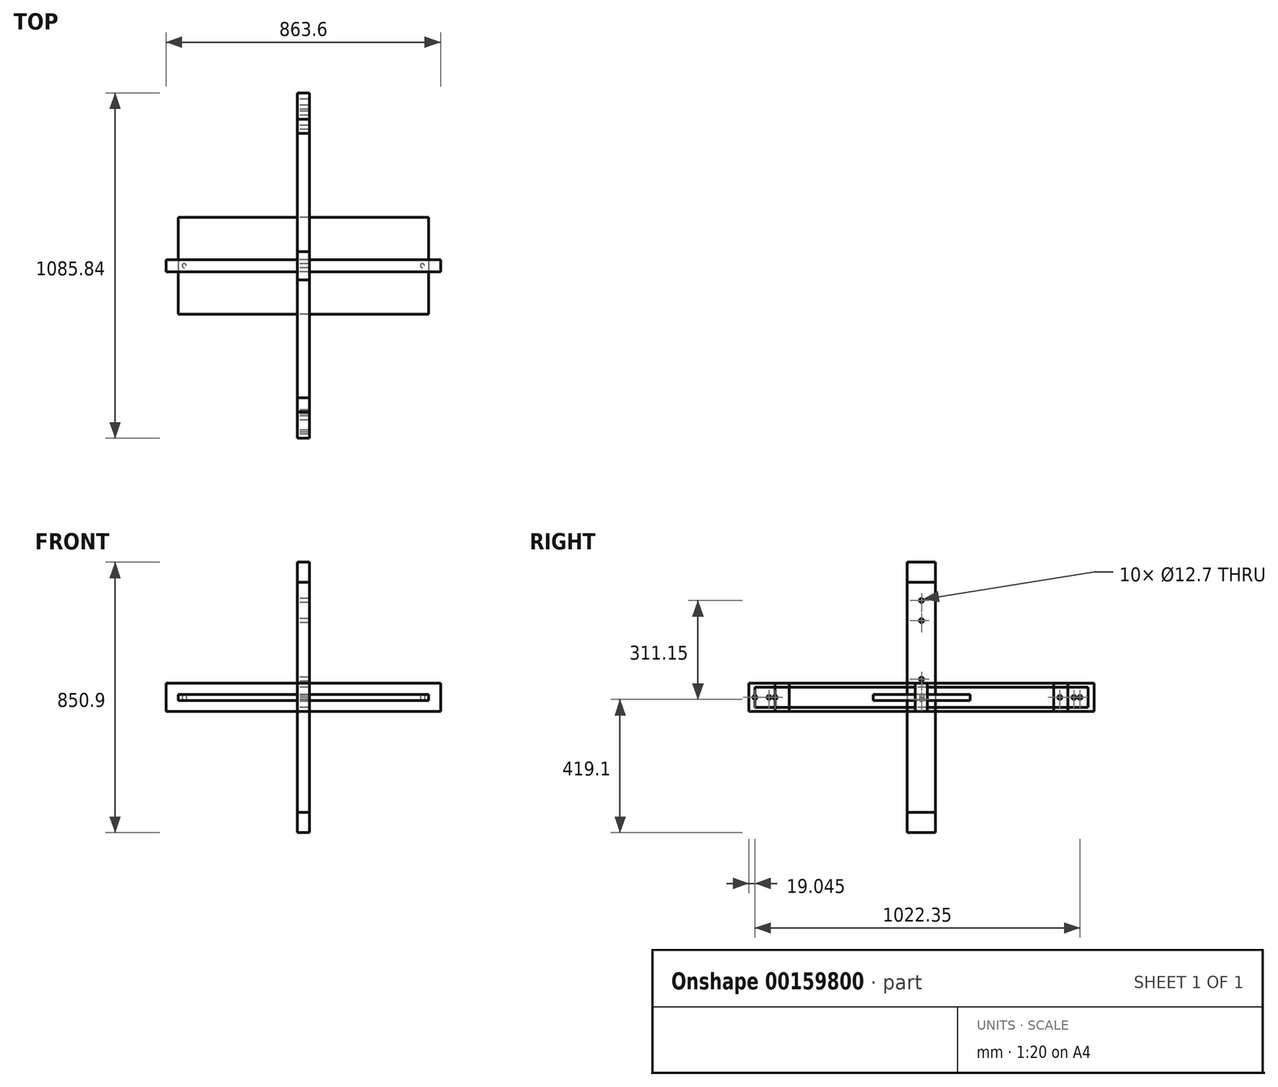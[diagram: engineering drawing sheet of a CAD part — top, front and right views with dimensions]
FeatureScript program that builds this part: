
annotation { "Feature Type Name" : "Feature", "Feature Type Description" : "" }
export const myFeature = defineFeature(function(context is Context, id is Id, definition is map)
    precondition{}
    {
        {
            var Q0;
            Q0=qCreatedBy(makeId("Front.planeOp"),FACE);
            var sketch = newSketch(context, id + "F0", { "sketchPlane" : qUnion([Q0])});
            skLineSegment(sketch, "E0.bottom", {"start": v(431.8, -44.45) * mm, "end": v(-431.8, -44.45) * mm});
            skLineSegment(sketch, "E0.top", {"start": v(431.8, 44.45) * mm, "end": v(-431.8, 44.45) * mm});
            skLineSegment(sketch, "E0.left", {"start": v(431.8, -44.45) * mm, "end": v(431.8, 44.45) * mm});
            skLineSegment(sketch, "E0.right", {"start": v(-431.8, -44.45) * mm, "end": v(-431.8, 44.45) * mm});
            skPoint(sketch, "E0.middle", {"position": v(0, 0) * mm});
            skSolve(sketch);
        }
        {
            var Q0;
            Q0 = qSketchRegion(id + "F0", true);
            extrude(context, id + "F1", {"entities" : qUnion([Q0]), "depth" : 38.1 * mm, "symmetric" : true});
        }
        {
            var Q0;
            Q0=qCreatedBy(makeId("Right.planeOp"),FACE);
            var sketch = newSketch(context, id + "F2", { "sketchPlane" : qUnion([Q0])});
            skLineSegment(sketch, "E1.bottom", {"start": v(542.93, -44.45) * mm, "end": v(-542.93, -44.45) * mm});
            skLineSegment(sketch, "E1.top", {"start": v(542.93, 44.45) * mm, "end": v(-542.93, 44.45) * mm});
            skLineSegment(sketch, "E1.left", {"start": v(542.93, -44.45) * mm, "end": v(542.93, 44.45) * mm});
            skLineSegment(sketch, "E1.right", {"start": v(-542.93, -44.45) * mm, "end": v(-542.93, 44.45) * mm});
            skPoint(sketch, "E1.middle", {"position": v(0, 0) * mm});
            skCircle(sketch, "E2", {"center": v(-523.88, 0) * mm, "radius": 6.35 * mm});
            skCircle(sketch, "E3", {"center": v(-460.38, 0) * mm, "radius": 6.35 * mm});
            skCircle(sketch, "E4", {"center": v(498.48, 0) * mm, "radius": 6.35 * mm});
            skPoint(sketch, "E4.centerSnap0", {"position": v(542.93, 0) * mm});
            skCircle(sketch, "E5", {"center": v(434.98, 0) * mm, "radius": 6.35 * mm});
            skSolve(sketch);
        }
        {
            var Q0;
            Q0 = qSketchRegion(id + "F2", true);
            extrude(context, id + "F3", {"entities" : qUnion([Q0]), "depth" : 38.1 * mm, "symmetric" : true});
        }
        {
            var Q0;
            Q0=qCreatedBy(makeId("Right.planeOp"),FACE);
            var sketch = newSketch(context, id + "F4", { "sketchPlane" : qUnion([Q0])});
            skLineSegment(sketch, "E6.bottom", {"start": v(-44.45, 361.95) * mm, "end": v(44.45, 361.95) * mm});
            skLineSegment(sketch, "E6.top", {"start": v(-44.45, -361.95) * mm, "end": v(44.45, -361.95) * mm});
            skLineSegment(sketch, "E6.left", {"start": v(-44.45, 361.95) * mm, "end": v(-44.45, -361.95) * mm});
            skLineSegment(sketch, "E6.right", {"start": v(44.45, 361.95) * mm, "end": v(44.45, -361.95) * mm});
            skPoint(sketch, "E6.middle", {"position": v(0, 0) * mm});
            skCircle(sketch, "E7", {"center": v(0, 304.8) * mm, "radius": 6.35 * mm});
            skCircle(sketch, "E8", {"center": v(0, 57.15) * mm, "radius": 6.35 * mm});
            skSolve(sketch);
        }
        {
            var Q0;
            Q0 = qSketchRegion(id + "F4", true);
            extrude(context, id + "F5", {"entities" : qUnion([Q0]), "depth" : 38.1 * mm, "symmetric" : true});
        }
        {
            var Q0;
            Q0=qCreatedBy(makeId("Right.planeOp"),FACE);
            var sketch = newSketch(context, id + "F6", { "sketchPlane" : qUnion([Q0])});
            skLineSegment(sketch, "E9.bottom", {"start": v(44.45, 425.45) * mm, "end": v(-44.45, 425.45) * mm});
            skLineSegment(sketch, "E9.top", {"start": v(44.45, -425.45) * mm, "end": v(-44.45, -425.45) * mm});
            skLineSegment(sketch, "E9.left", {"start": v(44.45, 425.45) * mm, "end": v(44.45, -425.45) * mm});
            skLineSegment(sketch, "E9.right", {"start": v(-44.45, 425.45) * mm, "end": v(-44.45, -425.45) * mm});
            skPoint(sketch, "E9.middle", {"position": v(0, 0) * mm});
            skCircle(sketch, "E10", {"center": v(0, 241.3) * mm, "radius": 6.35 * mm});
            skCircle(sketch, "E11", {"center": v(0, -6.35) * mm, "radius": 6.35 * mm});
            skSolve(sketch);
        }
        {
            var Q0;
            Q0 = qSketchRegion(id + "F6", true);
            extrude(context, id + "F7", {"entities" : qUnion([Q0]), "depth" : 38.1 * mm, "symmetric" : true});
        }
        {
            var Q0;
            Q0=qCreatedBy(makeId("Top.planeOp"),FACE);
            var sketch = newSketch(context, id + "F8", { "sketchPlane" : qUnion([Q0])});
            skLineSegment(sketch, "E12.bottom", {"start": v(393.7, 152.4) * mm, "end": v(-393.7, 152.4) * mm});
            skLineSegment(sketch, "E12.top", {"start": v(393.7, -152.4) * mm, "end": v(-393.7, -152.4) * mm});
            skLineSegment(sketch, "E12.left", {"start": v(393.7, 152.4) * mm, "end": v(393.7, -152.4) * mm});
            skLineSegment(sketch, "E12.right", {"start": v(-393.7, 152.4) * mm, "end": v(-393.7, -152.4) * mm});
            skPoint(sketch, "E12.middle", {"position": v(0, 0) * mm});
            skCircle(sketch, "E13", {"center": v(-374.65, 0) * mm, "radius": 6.35 * mm});
            skCircle(sketch, "E14", {"center": v(374.65, 0) * mm, "radius": 6.35 * mm});
            skPoint(sketch, "E14.centerSnap0", {"position": v(-393.7, 0) * mm});
            skSolve(sketch);
        }
        {
            var Q0;
            Q0 = qSketchRegion(id + "F8", true);
            extrude(context, id + "F9", {"entities" : qUnion([Q0]), "depth" : 19.05 * mm, "symmetric" : true});
        }
        {
            var Q0;
            Q0=qCreatedBy(makeId("Right.planeOp"),FACE);
            var sketch = newSketch(context, id + "F10", { "sketchPlane" : qUnion([Q0])});
            skLineSegment(sketch, "E15.bottom", {"start": v(523.88, -31.75) * mm, "end": v(-523.88, -31.75) * mm});
            skLineSegment(sketch, "E15.top", {"start": v(523.88, 31.75) * mm, "end": v(-523.88, 31.75) * mm});
            skLineSegment(sketch, "E15.left", {"start": v(523.88, -31.75) * mm, "end": v(523.88, 31.75) * mm});
            skLineSegment(sketch, "E15.right", {"start": v(-523.88, -31.75) * mm, "end": v(-523.88, 31.75) * mm});
            skPoint(sketch, "E15.middle", {"position": v(0, 0) * mm});
            skCircle(sketch, "E16", {"center": v(-479.43, 0) * mm, "radius": 6.35 * mm});
            skCircle(sketch, "E17", {"center": v(479.43, 0) * mm, "radius": 6.35 * mm});
            skPoint(sketch, "E17.centerSnap0", {"position": v(523.88, 0) * mm});
            skSolve(sketch);
        }
        {
            var Q0;
            Q0=makeQuery(id+"F10.imprint","IMPRINT",FACE,{"disambiguationData":[TD([[makeQuery(id+"F10.imprint","IMPRINT",EDGE,{"derivedFrom":sQuery(id+"F10.wireOp",EDGE,"E15.bottom")}),-1.0]])]});
            extrude(context, id + "F11", {"entities" : qUnion([Q0]), "depth" : 38.1 * mm, "symmetric" : true});
        }
        {
            var Q0;
            Q0=qCreatedBy(makeId("Right.planeOp"),FACE);
            var sketch = newSketch(context, id + "F12", { "sketchPlane" : qUnion([Q0])});
            skLineSegment(sketch, "E18.bottom", {"start": v(460.38, 44.45) * mm, "end": v(-460.38, 44.45) * mm});
            skLineSegment(sketch, "E18.top", {"start": v(460.38, -44.45) * mm, "end": v(-460.38, -44.45) * mm});
            skLineSegment(sketch, "E18.left", {"start": v(460.38, 44.45) * mm, "end": v(460.38, -44.45) * mm});
            skLineSegment(sketch, "E18.right", {"start": v(-460.38, 44.45) * mm, "end": v(-460.38, -44.45) * mm});
            skPoint(sketch, "E18.middle", {"position": v(0, 0) * mm});
            skSolve(sketch);
        }
        {
            var Q0;
            Q0=makeQuery(id+"F12.imprint","IMPRINT",FACE,{"disambiguationData":[TD([[makeQuery(id+"F12.imprint","IMPRINT",EDGE,{"derivedFrom":sQuery(id+"F12.wireOp",EDGE,"E18.bottom")}),1.0]])]});
            extrude(context, id + "F13", {"entities" : qUnion([Q0]), "depth" : 38.1 * mm, "symmetric" : true});
        }
        {
            var Q0;
            Q0=qCreatedBy(makeId("Right.planeOp"),FACE);
            var sketch = newSketch(context, id + "F14", { "sketchPlane" : qUnion([Q0])});
            skLineSegment(sketch, "E19.bottom", {"start": v(415.93, 44.45) * mm, "end": v(-415.93, 44.45) * mm});
            skLineSegment(sketch, "E19.top", {"start": v(415.93, -44.45) * mm, "end": v(-415.93, -44.45) * mm});
            skLineSegment(sketch, "E19.left", {"start": v(415.93, 44.45) * mm, "end": v(415.93, -44.45) * mm});
            skLineSegment(sketch, "E19.right", {"start": v(-415.93, 44.45) * mm, "end": v(-415.93, -44.45) * mm});
            skPoint(sketch, "E19.middle", {"position": v(0, 0) * mm});
            skSolve(sketch);
        }
        {
            var Q0;
            Q0 = qSketchRegion(id + "F14", true);
            extrude(context, id + "F15", {"entities" : qUnion([Q0]), "depth" : 38.1 * mm, "symmetric" : true});
        }
    });
